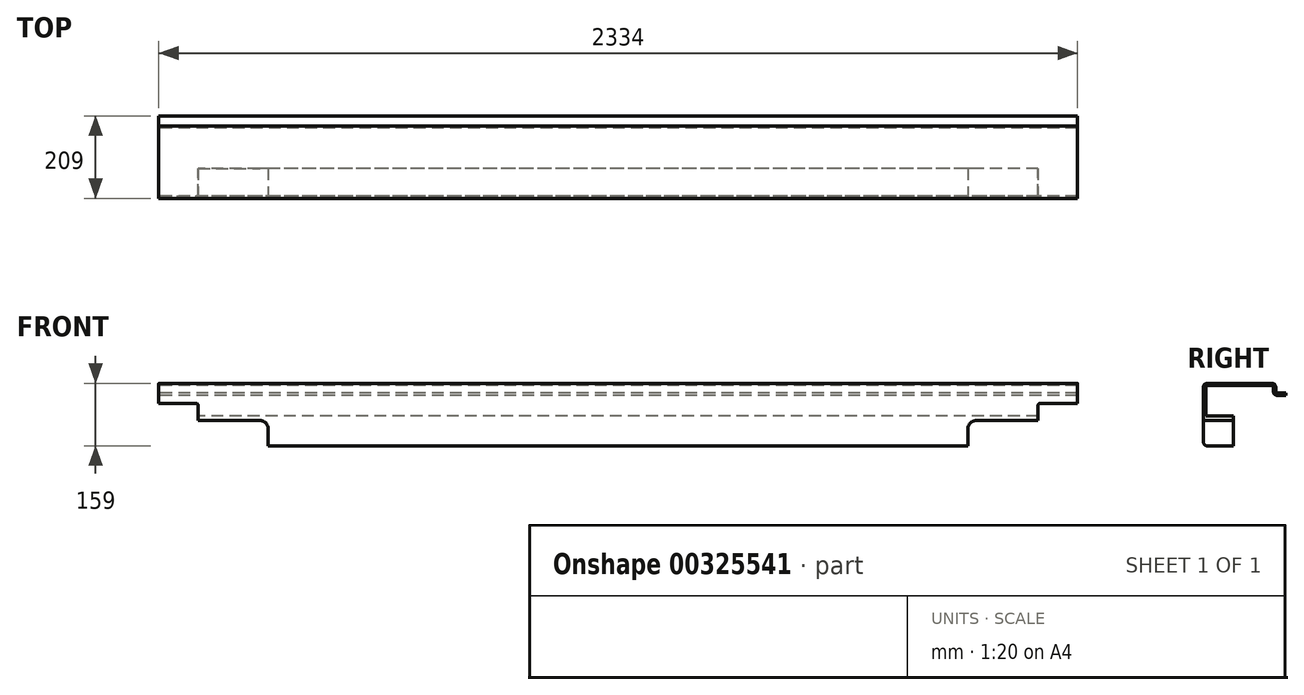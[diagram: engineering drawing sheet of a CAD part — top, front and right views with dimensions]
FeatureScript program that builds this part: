
annotation { "Feature Type Name" : "Feature", "Feature Type Description" : "" }
export const myFeature = defineFeature(function(context is Context, id is Id, definition is map)
    precondition{}
    {
        {
            var Q0;
            Q0=qCreatedBy(makeId("Right.planeOp"),FACE);
            var sketch = newSketch(context, id + "F0", { "sketchPlane" : qUnion([Q0])});
            skLineSegment(sketch, "E0", {"start": v(181.93, 119.63) * mm, "end": v(161.93, 119.63) * mm});
            skLineSegment(sketch, "E1", {"start": v(156.93, 124.63) * mm, "end": v(156.93, 134.63) * mm});
            skLineSegment(sketch, "E2", {"start": v(146.93, 144.63) * mm, "end": v(-17.07, 144.63) * mm});
            skLineSegment(sketch, "E3", {"start": v(-27.07, 134.63) * mm, "end": v(-27.07, -4.37) * mm});
            skLineSegment(sketch, "E4", {"start": v(-17.07, -14.37) * mm, "end": v(48.93, -14.37) * mm});
            skLineSegment(sketch, "E5", {"start": v(48.93, -14.37) * mm, "end": v(48.93, -8.37) * mm});
            skLineSegment(sketch, "E6", {"start": v(-21.07, 61.63) * mm, "end": v(-21.07, 133.63) * mm});
            skLineSegment(sketch, "E7", {"start": v(-16.07, 138.63) * mm, "end": v(145.93, 138.63) * mm});
            skLineSegment(sketch, "E8", {"start": v(150.93, 133.63) * mm, "end": v(150.93, 123.63) * mm});
            skLineSegment(sketch, "E9", {"start": v(160.93, 113.63) * mm, "end": v(181.93, 113.63) * mm});
            skLineSegment(sketch, "E10", {"start": v(181.93, 113.63) * mm, "end": v(181.93, 119.63) * mm});
            skPoint(sketch, "E11.visualSharp", {"position": v(156.93, 119.63) * mm});
            skArc(sketch, "E11.filletArc", {"start": v(156.93, 124.63) * mm, "mid": v(158.4, 121.09) * mm, "end": v(161.93, 119.63) * mm});
            skPoint(sketch, "E12.visualSharp", {"position": v(150.93, 138.63) * mm});
            skArc(sketch, "E12.filletArc", {"start": v(150.93, 133.63) * mm, "mid": v(149.46, 137.16) * mm, "end": v(145.93, 138.63) * mm});
            skPoint(sketch, "E13.visualSharp", {"position": v(-21.07, 138.63) * mm});
            skArc(sketch, "E13.filletArc", {"start": v(-16.07, 138.63) * mm, "mid": v(-19.6, 137.16) * mm, "end": v(-21.07, 133.63) * mm});
            skPoint(sketch, "E14.visualSharp", {"position": v(-21.07, -8.37) * mm});
            skPoint(sketch, "E15.visualSharp", {"position": v(156.93, 144.63) * mm});
            skArc(sketch, "E15.filletArc", {"start": v(156.93, 134.63) * mm, "mid": v(154, 141.7) * mm, "end": v(146.93, 144.63) * mm});
            skPoint(sketch, "E16.visualSharp", {"position": v(150.93, 113.63) * mm});
            skArc(sketch, "E16.filletArc", {"start": v(150.93, 123.63) * mm, "mid": v(153.86, 116.55) * mm, "end": v(160.93, 113.63) * mm});
            skPoint(sketch, "E17.visualSharp", {"position": v(-27.07, 144.63) * mm});
            skArc(sketch, "E17.filletArc", {"start": v(-17.07, 144.63) * mm, "mid": v(-24.14, 141.7) * mm, "end": v(-27.07, 134.63) * mm});
            skPoint(sketch, "E18.visualSharp", {"position": v(-27.07, -14.37) * mm});
            skArc(sketch, "E18.filletArc", {"start": v(-27.07, -4.37) * mm, "mid": v(-24.14, -11.45) * mm, "end": v(-17.07, -14.37) * mm});
            skLineSegment(sketch, "E19", {"start": v(48.93, -14.37) * mm, "end": v(48.93, 61.63) * mm});
            skLineSegment(sketch, "E20", {"start": v(48.93, 61.63) * mm, "end": v(-27.07, 61.63) * mm});
            skSolve(sketch);
        }
        {
            var Q0;
            Q0 = qSketchRegion(id + "F0", true);
            extrude(context, id + "F1", {"entities" : qUnion([Q0]), "depth" : 2334 * mm});
        }
        {
            var Q0;
            Q0=makeQuery(id+"F1.opExtrude","SWEPT_FACE",FACE,{"disambiguationData":[OSD([sQuery(id+"F0.wireOp",EDGE,"E3")])]});
            var sketch = newSketch(context, id + "F2", { "sketchPlane" : qUnion([Q0])});
            skLineSegment(sketch, "E21", {"start": v(0, 93.63) * mm, "end": v(95, 93.63) * mm});
            skLineSegment(sketch, "E22", {"start": v(100, 88.63) * mm, "end": v(100, 49.63) * mm});
            skLineSegment(sketch, "E23", {"start": v(100, 49.63) * mm, "end": v(258, 49.63) * mm});
            skLineSegment(sketch, "E24.MirrorCS", {"start": v(2234, 88.63) * mm, "end": v(2234, 49.63) * mm});
            skLineSegment(sketch, "E25.MirrorCS", {"start": v(2056, 29.63) * mm, "end": v(2056, -14.37) * mm});
            skLineSegment(sketch, "E26.MirrorCS", {"start": v(2234, 49.63) * mm, "end": v(2076, 49.63) * mm});
            skLineSegment(sketch, "E27.MirrorCS", {"start": v(2334, 93.63) * mm, "end": v(2239, 93.63) * mm});
            skLineSegment(sketch, "E28", {"start": v(278, 29.63) * mm, "end": v(278, -30.37) * mm});
            skLineSegment(sketch, "E29", {"start": v(278, -30.37) * mm, "end": v(0, -30.37) * mm});
            skLineSegment(sketch, "E30", {"start": v(0, -30.37) * mm, "end": v(0, 93.63) * mm});
            skLineSegment(sketch, "E31", {"start": v(2056, -14.37) * mm, "end": v(2056, -32.3) * mm});
            skLineSegment(sketch, "E32", {"start": v(2056, -32.3) * mm, "end": v(2334, -32.3) * mm});
            skLineSegment(sketch, "E33", {"start": v(2334, -32.3) * mm, "end": v(2334, 93.63) * mm});
            skPoint(sketch, "E34.visualSharp", {"position": v(100, 93.63) * mm});
            skArc(sketch, "E34.filletArc", {"start": v(100, 88.63) * mm, "mid": v(98.54, 92.16) * mm, "end": v(95, 93.63) * mm});
            skPoint(sketch, "E35.visualSharp", {"position": v(2234, 93.63) * mm});
            skArc(sketch, "E35.filletArc", {"start": v(2239, 93.63) * mm, "mid": v(2235.46, 92.16) * mm, "end": v(2234, 88.63) * mm});
            skPoint(sketch, "E36.visualSharp", {"position": v(2056, 49.63) * mm});
            skArc(sketch, "E36.filletArc", {"start": v(2076, 49.63) * mm, "mid": v(2061.86, 43.77) * mm, "end": v(2056, 29.63) * mm});
            skPoint(sketch, "E37.visualSharp", {"position": v(278, 49.63) * mm});
            skArc(sketch, "E37.filletArc", {"start": v(278, 29.63) * mm, "mid": v(272.14, 43.77) * mm, "end": v(258, 49.63) * mm});
            skSolve(sketch);
        }
        {
            var Q0;
            {var subQ0=sQuery(id+"F2.wireOp",EDGE,"E29");Q0=makeQuery(id+"F2.imprint","IMPRINT",FACE,{"disambiguationData":[TD([[makeQuery(id+"F2.imprint","IMPRINT",EDGE,{"derivedFrom":subQ0}),-1.0]])]});}
            var Q1;
            {var subQ6=sQuery(id+"F2.wireOp",EDGE,"E21");Q1=makeQuery(id+"F2.imprint","IMPRINT",FACE,{"disambiguationData":[TD([[makeQuery(id+"F2.imprint","IMPRINT",EDGE,{"derivedFrom":subQ6}),-1.0]])]});}
            extrude(context, id + "F3", {"entities" : qUnion([Q0, Q1]), "operationType" : NewBodyOperationType.REMOVE, "oppositeDirection" : true, "depth" : 80 * mm});
        }
        {
            var Q0;
            Q0=makeQuery(id+"F2.imprint","IMPRINT",FACE,{"disambiguationData":[TD([[makeQuery(id+"F2.imprint","IMPRINT",EDGE,{"derivedFrom":sQuery(id+"F2.wireOp",EDGE,"E24.MirrorCS")}),1.0]])]});
            var Q1;
            {var subQ4=sQuery(id+"F2.wireOp",EDGE,"E31");Q1=makeQuery(id+"F2.imprint","IMPRINT",FACE,{"disambiguationData":[TD([[makeQuery(id+"F2.imprint","IMPRINT",EDGE,{"derivedFrom":subQ4}),1.0]])]});}
            extrude(context, id + "F4", {"entities" : qUnion([Q0, Q1]), "operationType" : NewBodyOperationType.REMOVE, "oppositeDirection" : true, "depth" : 80 * mm});
        }
    });
